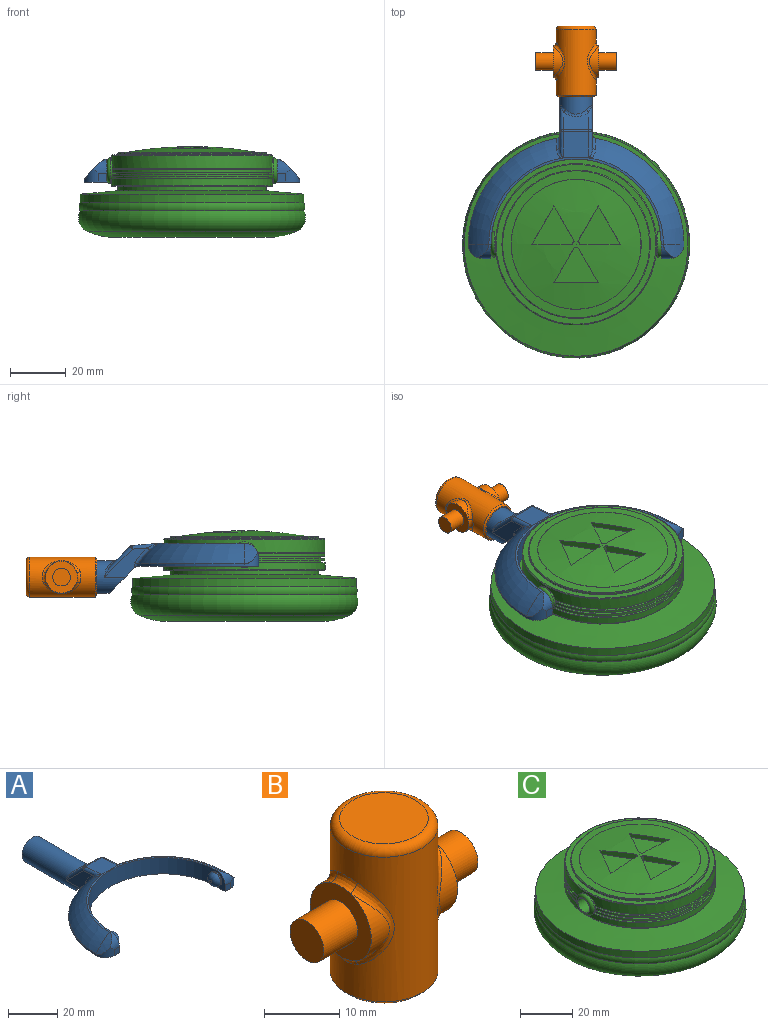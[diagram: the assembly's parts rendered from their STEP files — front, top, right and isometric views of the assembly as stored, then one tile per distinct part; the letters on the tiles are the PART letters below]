
ASSEMBLY  parts=3 mates=2
PART A: 48 faces, bbox 77.3x80.8x18.2 mm
  f0: plane 11.99x9.83mm, normal (0,-0.71,-0.71), area 141.5mm2, adj f1,f2,f9,f30,f43,f46
  f1: plane 15.39x10.49mm, normal (-1,0,0), area 63.5mm2, adj f0,f30,f32,f36,f46,f47
  f2: plane 15.39x10.49mm, normal (1,0,0), area 63.5mm2, adj f0,f30,f34,f39,f43,f44
  f3: plane 9.14x6.37mm, normal (0,0.71,0.71), area 67.6mm2, adj f35,f36,f39,f40
  f4: cylinder r=38.61mm len=37.99mm, axis (0,0,-1), area 42.6mm2, adj f6,f9,f17,f46,f47
  f5: torus R=19.3mm, axis (0,0,-1), area 507.8mm2, adj f10,f11,f12,f29,f42,f44
  f6: torus R=19.3mm, axis (0,0,-1), area 507.8mm2, adj f4,f11,f15,f28,f45,f47
  f7: cylinder r=30.48mm len=60.96mm, axis (0,0,-1), area 746.6mm2, adj f8,f9,f11,f14,f21,f24
  f8: plane 8.13x5.08mm, normal (-1,0,0), area 19.9mm2, adj f7,f9,f13,f19,f24
  f9: plane 77.22x43.73mm, normal (0,0,-1), area 956.2mm2, adj f0,f4,f7,f8,f10,f13,f14,f16
  f10: cylinder r=38.61mm len=37.99mm, axis (0,0,-1), area 42.6mm2, adj f5,f9,f20,f43,f44
  f11: plane 62.55x30.95mm, normal (0,0,1), area 75mm2, adj f5,f6,f7,f18,f19,f27
  f12: cylinder r=22.71mm len=7.33mm, axis (0,1,0), area 24.8mm2, adj f5,f19,f20
  f13: plane 3.05x3.05mm, normal (0,-1,0), area 9.3mm2, adj f8,f9,f19,f20
  f14: plane 8.13x5.08mm, normal (1,0,0), area 19.9mm2, adj f7,f9,f16,f18,f21
  f15: cylinder r=22.71mm len=7.33mm, axis (0,1,0), area 24.8mm2, adj f6,f17,f18
  f16: plane 3.05x3.05mm, normal (0,-1,0), area 9.3mm2, adj f9,f14,f17,f18
  f17: cylinder r=5.08mm len=5.08mm, axis (0,0,-1), area 21.9mm2, adj f4,f9,f15,f16,f18
  f18: cylinder r=5.08mm len=5.08mm, axis (-1,0,0), area 21.9mm2, adj f11,f14,f15,f16,f17
  f19: cylinder r=5.08mm len=5.08mm, axis (-1,0,0), area 21.9mm2, adj f8,f11,f12,f13,f20
  f20: cylinder r=5.08mm len=5.08mm, axis (0,0,-1), area 21.9mm2, adj f9,f10,f12,f13,f19
  f21: cylinder r=3.17mm len=6.35mm, axis (-1,0,0), area 12.7mm2, adj f7,f14,f23
  f22: plane 1.27x1.27mm, normal (1,0,0), area 1.3mm2, adj f23
  f23: torus R=0.64mm, axis (1,0,0), area 56.5mm2, adj f21,f22
  f24: cylinder r=3.17mm len=6.35mm, axis (1,0,0), area 12.7mm2, adj f7,f8,f26
  f25: plane 1.27x1.27mm, normal (-1,0,0), area 1.3mm2, adj f26
  f26: torus R=0.64mm, axis (-1,0,0), area 56.5mm2, adj f24,f25
  f27: plane 9.86x9.36mm, normal (0,0.09,1), area 85.6mm2, adj f11,f28,f29,f32,f34,f35,f42,f45
  f28: plane 1.04x0.17mm, normal (0,-1,0), area 0mm2, adj f6,f27,f45
  f29: plane 1.04x0.17mm, normal (0,-1,0), area 0mm2, adj f5,f27,f42
  f30: cylinder r=5.84mm len=33.01mm, axis (0,-1,0), area 1029.7mm2, adj f0,f1,f2,f31,f38,f40,f41
  f31: plane 11.68x11.68mm, normal (0,1,0), area 107.2mm2, adj f30
  f32: cylinder r=1.27mm len=9.13mm, axis (0,-1,0.09), area 14.4mm2, adj f1,f27,f33,f45
  f33: sphere r=1.27mm, area 1.5mm2, adj f32,f35,f36
  f34: cylinder r=1.27mm len=9.13mm, axis (0,1,-0.09), area 14.4mm2, adj f2,f27,f37,f42
  f35: cylinder r=1.27mm len=9.14mm, axis (-1,0,0), area 8.1mm2, adj f3,f27,f33,f37
  f36: cylinder r=1.27mm len=10.91mm, axis (0,-0.71,0.71), area 23.1mm2, adj f1,f3,f33,f38
  f37: sphere r=1.27mm, area 1.5mm2, adj f34,f35,f39
  f38: bspline ~4.55x2.75mm, area 2.3mm2, adj f30,f36,f40
  f39: cylinder r=1.27mm len=10.91mm, axis (0,0.71,-0.71), area 23.1mm2, adj f2,f3,f37,f41
  f40: bspline ~9.14x2.56mm, area 10.7mm2, adj f3,f30,f38,f41
  f41: bspline ~5.23x3.53mm, area 2.3mm2, adj f30,f39,f40
  f42: bspline ~4.62x3.14mm, area 5.2mm2, adj f5,f27,f29,f34,f44
  f43: cylinder r=1.27mm len=1.74mm, axis (0,0,-1), area 1.9mm2, adj f0,f2,f9,f10,f44
  f44: bspline ~8.6x7.86mm, area 11.9mm2, adj f2,f5,f10,f42,f43
  f45: bspline ~4.62x3.14mm, area 5.2mm2, adj f6,f27,f28,f32,f47
  f46: cylinder r=1.27mm len=1.74mm, axis (0,0,-1), area 1.9mm2, adj f0,f1,f4,f9,f47
  f47: bspline ~8.6x7.86mm, area 11.9mm2, adj f1,f4,f6,f45,f46
PART B: 25 faces, bbox 28.9x15.5x25.4 mm
  f0: cylinder r=5.71mm len=10.81mm, axis (-1,0,0), area 26.2mm2, adj f5,f15
  f1: cylinder r=5.71mm len=10.81mm, axis (-1,0,0), area 26.2mm2, adj f8,f11
  f2: cylinder r=7.14mm len=23.5mm, axis (0,0,-1), area 763.2mm2, adj f9,f10,f11,f12,f13,f14,f15,f16
  f3: plane 11.75x11.75mm, normal (0,0,1), area 108.4mm2, adj f17
  f4: plane 13.02x13.02mm, normal (0,0,-1), area 16.3mm2, adj f22,f24
  f5: plane 11.46x11.46mm, normal (1,0,0), area 70.9mm2, adj f0,f6,f13,f16,f18
  f6: cylinder r=5.71mm len=10.81mm, axis (-1,0,0), area 26.2mm2, adj f5,f14
  f7: cylinder r=5.71mm len=10.81mm, axis (-1,0,0), area 26.2mm2, adj f8,f10
  f8: plane 11.46x11.46mm, normal (-1,0,0), area 70.9mm2, adj f1,f7,f9,f12,f20
  f9: bspline ~4.64x1.73mm, area 6.5mm2, adj f2,f8,f10,f11
  f10: bspline ~13.62x4.91mm, area 20.7mm2, adj f2,f7,f9,f12
  f11: bspline ~13.6x4.87mm, area 20.7mm2, adj f1,f2,f9,f12
  f12: bspline ~4.64x1.73mm, area 6.5mm2, adj f2,f8,f10,f11
  f13: bspline ~4.64x1.73mm, area 6.5mm2, adj f2,f5,f14,f15
  f14: bspline ~13.62x4.91mm, area 20.7mm2, adj f2,f6,f13,f16
  f15: bspline ~13.6x4.87mm, area 20.7mm2, adj f0,f2,f13,f16
  f16: bspline ~4.64x1.73mm, area 6.5mm2, adj f2,f5,f14,f15
  f17: torus R=5.87mm, axis (0,0,1), area 83.8mm2, adj f2,f3
  f18: cylinder r=3.17mm len=6.35mm, axis (-1,0,0), area 126.7mm2, adj f5,f19
  f19: plane 6.35x6.35mm, normal (1,0,0), area 31.7mm2, adj f18
  f20: cylinder r=3.17mm len=6.35mm, axis (1,0,0), area 126.7mm2, adj f8,f21
  f21: plane 6.35x6.35mm, normal (-1,0,0), area 31.7mm2, adj f20
  f22: cylinder r=6.1mm len=22.86mm, axis (0,0,-1), area 875.6mm2, adj f4,f23
  f23: plane 12.19x12.19mm, normal (0,0,-1), area 116.7mm2, adj f22
  f24: cone r=7.14mm half-angle=45deg, axis (0,0,1), area 38.5mm2, adj f2,f4
PART C: 63 faces, bbox 96.2x96.2x32.5 mm
  f0: cylinder r=28.87mm len=57.73mm, axis (0,0,-1), area 436.4mm2, adj f3,f4,f53,f54,f59
  f1: plane 57.18x24.88mm, normal (0,0,-1), area 102.5mm2, adj f6,f8,f53,f54
  f2: plane 57.18x24.88mm, normal (0,0,-1), area 102.5mm2, adj f5,f7,f53,f54
  f3: plane 57.29x25.3mm, normal (0,0,1), area 103.6mm2, adj f0,f6,f53,f54
  f4: plane 57.29x25.3mm, normal (0,0,1), area 103.6mm2, adj f0,f5,f53,f54
  f5: cylinder r=27.6mm len=54.73mm, axis (0,0,-1), area 50.2mm2, adj f2,f4,f53,f54
  f6: cylinder r=27.6mm len=54.73mm, axis (0,0,-1), area 50.2mm2, adj f1,f3,f53,f54
  f7: cylinder r=28.87mm len=57.18mm, axis (0,0,-1), area 78.4mm2, adj f2,f13,f53,f54
  f8: cylinder r=28.87mm len=57.18mm, axis (0,0,-1), area 78.4mm2, adj f1,f14,f53,f54
  f9: cylinder r=27.6mm len=54.49mm, axis (0,0,-1), area 49.4mm2, adj f11,f13,f53,f54
  f10: cylinder r=27.6mm len=54.49mm, axis (0,0,-1), area 49.4mm2, adj f12,f14,f53,f54
  f11: plane 57.02x24.34mm, normal (0,0,-1), area 101.1mm2, adj f9,f15,f53,f54
  f12: plane 57.02x24.34mm, normal (0,0,-1), area 101.1mm2, adj f10,f16,f53,f54
  f13: plane 57.06x24.48mm, normal (0,0,1), area 101.4mm2, adj f7,f9,f53,f54
  f14: plane 57.06x24.48mm, normal (0,0,1), area 101.4mm2, adj f8,f10,f53,f54
  f15: cylinder r=28.87mm len=57.02mm, axis (0,0,-1), area 77.7mm2, adj f11,f20,f53,f54
  f16: cylinder r=28.87mm len=57.02mm, axis (0,0,-1), area 77.7mm2, adj f12,f19,f53,f54
  f17: plane 57.04x24.39mm, normal (0,0,-1), area 101.2mm2, adj f22,f23,f53,f54
  f18: plane 57.04x24.39mm, normal (0,0,-1), area 101.2mm2, adj f21,f23,f53,f54
  f19: plane 57.01x24.31mm, normal (0,0,1), area 101mm2, adj f16,f22,f53,f54
  f20: plane 57.01x24.31mm, normal (0,0,1), area 101mm2, adj f15,f21,f53,f54
  f21: cylinder r=27.6mm len=54.46mm, axis (0,0,-1), area 49.3mm2, adj f18,f20,f53,f54
  f22: cylinder r=27.6mm len=54.46mm, axis (0,0,-1), area 49.3mm2, adj f17,f19,f53,f54
  f23: cylinder r=28.87mm len=57.73mm, axis (0,0,-1), area 753.4mm2, adj f17,f18,f53,f54,f60
  f24: sphere r=135.39mm, area 1385.3mm2, adj f37,f38,f39,f40,f42,f43,f44,f45
  f25: plane 39.33x39.33mm, normal (0,0,-1), area 1214.6mm2, adj f26
  f26: torus R=20.12mm, axis (0,0,-1), area 1429.3mm2, adj f25,f27
  f27: torus R=27.74mm, axis (0,0,-1), area 3542.1mm2, adj f26,f28
  f28: torus R=35.36mm, axis (0,0,-1), area 2180.1mm2, adj f27,f29
  f29: torus R=37.35mm, axis (0,0,-1), area 734.6mm2, adj f28,f30
  f30: cylinder r=40.06mm len=80.11mm, axis (0,0,-1), area 799.1mm2, adj f29,f31
  f31: cone r=26.57mm half-angle=85deg, axis (0,0,-1), area 2833.8mm2, adj f30,f32
  f32: cylinder r=26.57mm len=53.14mm, axis (0,0,-1), area 265mm2, adj f31,f33
  f33: plane 57.23x57.23mm, normal (0,0,-1), area 354.5mm2, adj f32,f59
  f34: cone r=26.57mm half-angle=87deg, axis (0,0,-1), area 475.4mm2, adj f61,f62
  f35: cylinder r=26.57mm len=53.14mm, axis (0,0,-1), area 92.3mm2, adj f36,f61
  f36: plane 57.23x57.23mm, normal (0,0,1), area 354.5mm2, adj f35,f60
  f37: cylinder r=1.27mm len=2.53mm, axis (0,0,1), area 3.4mm2, adj f24,f38,f40,f41
  f38: plane 12.65x7.3mm, normal (-0.87,-0.5,0), area 32.2mm2, adj f24,f37,f39,f41
  f39: plane 13.75x7.94mm, normal (0.87,-0.5,0), area 28mm2, adj f24,f38,f40,f41
  f40: plane 14.61x2.53mm, normal (0,1,0), area 32.2mm2, adj f24,f37,f39,f41
  f41: plane 15.24x13.75mm, normal (0,0,1), area 108.3mm2, adj f37,f38,f39,f40
  f42: cylinder r=1.27mm len=2.53mm, axis (0,0,1), area 3.4mm2, adj f24,f43,f45,f46
  f43: plane 12.65x7.3mm, normal (0.87,-0.5,0), area 32.2mm2, adj f24,f42,f44,f46
  f44: plane 15.88x1.84mm, normal (0,1,0), area 28mm2, adj f24,f43,f45,f46
  f45: plane 12.65x7.3mm, normal (-0.87,-0.5,0), area 32.2mm2, adj f24,f42,f44,f46
  f46: plane 15.88x12.65mm, normal (0,0,1), area 108.3mm2, adj f42,f43,f44,f45
  f47: cylinder r=1.27mm len=2.53mm, axis (0,0,1), area 3.4mm2, adj f24,f48,f50,f51
  f48: plane 14.61x2.53mm, normal (0,1,0), area 32.2mm2, adj f24,f47,f49,f51
  f49: plane 13.75x7.94mm, normal (-0.87,-0.5,0), area 28mm2, adj f24,f48,f50,f51
  f50: plane 12.65x7.3mm, normal (0.87,-0.5,0), area 32.2mm2, adj f24,f47,f49,f51
  f51: plane 15.24x13.75mm, normal (0,0,1), area 108.3mm2, adj f47,f48,f49,f50
  f52: plane 6.6x6.6mm, normal (1,0,0), area 2.6mm2, adj f57,f58
  f53: cylinder r=4.57mm len=9.14mm, axis (-1,0,0), area 20.4mm2, adj f0,f1,f2,f3,f4,f5,f6,f7
  f54: cylinder r=4.57mm len=9.14mm, axis (-1,0,0), area 20.4mm2, adj f0,f1,f2,f3,f4,f5,f6,f7
  f55: plane 6.6x6.6mm, normal (-1,0,0), area 2.6mm2, adj f56,f58
  f56: torus R=3.3mm, axis (1,0,0), area 51.5mm2, adj f54,f55
  f57: torus R=3.3mm, axis (1,0,0), area 51.5mm2, adj f52,f53
  f58: cylinder r=3.17mm len=60.96mm, axis (1,0,0), area 1216.1mm2, adj f52,f55
  f59: torus R=28.61mm, axis (0,0,1), area 72.1mm2, adj f0,f33
  f60: torus R=28.61mm, axis (0,0,-1), area 72.1mm2, adj f23,f36
  f61: torus R=26.31mm, axis (0,0,1), area 64.2mm2, adj f34,f35
  f62: torus R=23.29mm, axis (0,0,1), area 4.5mm2, adj f24,f34
PLACE A t=(32.34,27.52,20.85)mm
PLACE B rot(axis=(-1,0,0),90deg) t=(32.34,80.3,16.88)mm
PLACE C t=(32.34,27.52,33.52)mm
MATE revolute A.f24 <-> C.f53  axis (-1,0,0) through (62.82,27.52,24.92)mm
MATE revolute B.f2 <-> A.f30  axis (0,-1,0) through (32.34,103.16,16.88)mm
